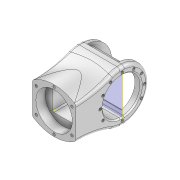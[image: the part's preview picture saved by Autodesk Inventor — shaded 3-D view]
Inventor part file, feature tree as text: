
AUTODESK INVENTOR PART (.ipt)
format: ipt  version: 2020.3 (Build 243373010, 373A)  size: 556,032 bytes
history: native  units: mm
features: sketch x10, extrude x7, fillet x3, hole x3, plane x2, projected_geometry x2, chamfer x1, mirror x1
ambient origin geometry x8: Origin, YZ Plane, XZ Plane, XY Plane, X Axis, Y Axis, Z Axis, Center Point
bodies: Solid1 (feature_tree)
feature tree (29):
  sketch  "Sketch1"  dims[d1=52.5mm d2=-35.0mm]
  plane  "Work Plane1"
  extrude  "Extrusion1"  [1 undecoded]
  extrude  "Extrusion2"  Depth=82.5mm
  extrude  "Extrusion4"  Depth=10.0mm
  fillet  "Fillet2"  Radius=70.0mm
  fillet  "Fillet3"  Radius=10.0mm
  fillet  "Fillet4"  Radius=35.0mm
  extrude  "Extrusion5"  Depth=60.0mm
  extrude  "Extrusion6"  Depth=10.0mm TaperAngle=0.0deg
  chamfer  "Chamfer1"  Distance=50.0mm
  sketch  "Sketch7"  dims[d21=72.0mm]
  hole  "Hole1"  [1 undecoded]
  hole  "Hole2"  [1 undecoded]
  sketch  "Sketch8"  dims[d22=68.5mm]
  hole  "Hole3"  [1 undecoded]
  mirror  "Mirror1"
  extrude  "Extrusion7"  Depth=10.0mm
  plane  "Work Plane2"
  extrude  "Extrusion8"  Depth=10.0mm
  sketch  "Sketch2"  dims[d3=37.5mm d4=82.5mm]
  sketch  "Sketch4"  dims[d5=82.5mm d6=12.5mm d7=70.0mm d8=0.0mm d9=10.0mm d10=0.0mm d13=35.0mm]
  projected_geometry  "Projected Loop1"
  sketch  "Sketch5"  dims[d14=50.0mm d16=70.0mm d17=60.0mm]
  sketch  "Sketch6"  dims[d18=60.0mm d19=10.0mm d20=0.0mm]
  sketch  "Sketch9"  dims[d23=5.0mm]
  sketch  "Sketch11"  dims[d24=5.0mm d25=50.0mm d26=0.0mm]
  sketch  "Sketch15"  dims[d27=3.054326mm d29=3.054326mm d30=50.0mm d31=0.0mm d32=2.0mm d33=2.0mm d34=45.0deg d36=35.0mm d38=4.134mm d39=10.0mm d40=7.0mm d41=2.0mm d42=90.0deg d43=14.2mm d44=20.594885mm d45=4.134mm d46=10.0mm d47=7.0mm d48=2.0mm d49=90.0deg d50=14.2mm d51=20.594885mm d52=6.108652mm d53=6.108652mm d56=12.217305mm d58=19.198622mm d59=19.198622mm d60=12.217305mm d61=35.0mm d62=35.0mm d63=35.0mm d64=3.531181mm d65=1.76559mm d66=36.207159mm d68=33.457159mm d69=7.5mm d71=30.707159mm d72=20.0mm d74=360.0deg d76=5.5mm d78=35.5mm d79=30.0mm d81=60.0deg d83=30.0mm d85=60.0deg d87=4.134mm d88=5.0mm d89=4.0mm d90=2.0mm d91=90.0deg d92=7.25mm d93=0.0mm d94=58.6mm d95=15.0mm d96=0.0mm d97=33.0mm d98=33.0mm d100=10.0mm d101=0.0mm d102=0.5mm d103=0.872665mm]
  projected_geometry  "Project Cut Edges1"
note: 4 required parameter values undecoded (feature->parameter linkage not recoverable at this tier; creation-order binding heuristic only, values carry confidence <= 0.55)
